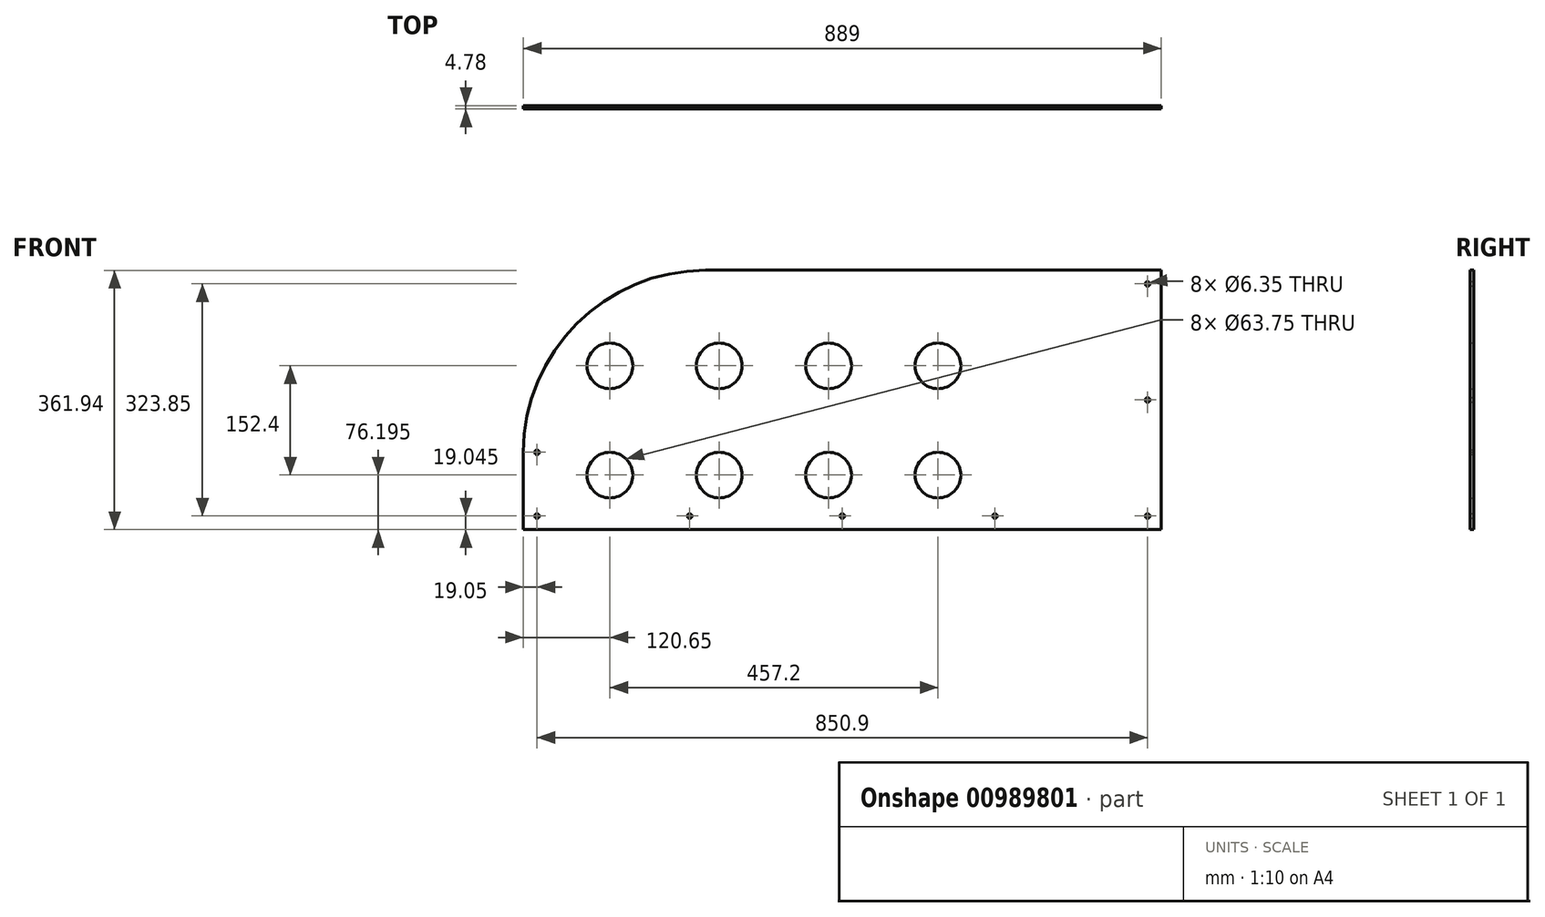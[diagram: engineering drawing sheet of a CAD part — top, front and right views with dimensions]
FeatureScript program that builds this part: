
annotation { "Feature Type Name" : "Feature", "Feature Type Description" : "" }
export const myFeature = defineFeature(function(context is Context, id is Id, definition is map)
    precondition{}
    {
        {
            var Q0;
            Q0=qCreatedBy(makeId("Front.planeOp"),FACE);
            var sketch = newSketch(context, id + "F0", { "sketchPlane" : qUnion([Q0])});
            skLineSegment(sketch, "E0.bottom", {"start": v(-190.5, 180.98) * mm, "end": v(444.5, 180.98) * mm});
            skLineSegment(sketch, "E0.top", {"start": v(-444.5, -180.98) * mm, "end": v(444.5, -180.98) * mm});
            skLineSegment(sketch, "E0.left", {"start": v(-444.5, -73.02) * mm, "end": v(-444.5, -180.98) * mm});
            skLineSegment(sketch, "E0.right", {"start": v(444.5, 180.98) * mm, "end": v(444.5, -180.98) * mm});
            skCircle(sketch, "E1", {"center": v(-323.85, 47.62) * mm, "radius": 31.88 * mm});
            skCircle(sketch, "E2.0.1.0", {"center": v(-323.85, -104.78) * mm, "radius": 31.88 * mm});
            skCircle(sketch, "E2.1.0.0", {"center": v(-171.45, 47.62) * mm, "radius": 31.88 * mm});
            skCircle(sketch, "E2.1.1.0", {"center": v(-171.45, -104.78) * mm, "radius": 31.88 * mm});
            skCircle(sketch, "E2.2.0.0", {"center": v(-19.05, 47.62) * mm, "radius": 31.88 * mm});
            skCircle(sketch, "E2.2.1.0", {"center": v(-19.05, -104.78) * mm, "radius": 31.88 * mm});
            skCircle(sketch, "E2.3.0.0", {"center": v(133.35, 47.62) * mm, "radius": 31.88 * mm});
            skCircle(sketch, "E2.3.1.0", {"center": v(133.35, -104.78) * mm, "radius": 31.88 * mm});
            skLineSegment(sketch, "E2.direction1", {"start": v(-323.85, 47.62) * mm, "end": v(-171.45, 47.62) * mm, "construction": true});
            skLineSegment(sketch, "E2.direction2", {"start": v(-323.85, 47.62) * mm, "end": v(-323.85, -104.78) * mm, "construction": true});
            skPoint(sketch, "E3.visualSharp", {"position": v(-444.5, 180.98) * mm});
            skArc(sketch, "E3.filletArc", {"start": v(-190.5, 180.98) * mm, "mid": v(-370.1, 106.58) * mm, "end": v(-444.5, -73.02) * mm});
            skCircle(sketch, "E4", {"center": v(-425.45, -161.92) * mm, "radius": 3.18 * mm});
            skCircle(sketch, "E5.1.0.0", {"center": v(-212.73, -161.92) * mm, "radius": 3.18 * mm});
            skCircle(sketch, "E5.2.0.0", {"center": v(0, -161.92) * mm, "radius": 3.18 * mm});
            skCircle(sketch, "E5.3.0.0", {"center": v(212.72, -161.92) * mm, "radius": 3.18 * mm});
            skCircle(sketch, "E5.4.0.0", {"center": v(425.45, -161.92) * mm, "radius": 3.18 * mm});
            skLineSegment(sketch, "E5.direction1", {"start": v(-425.45, -161.92) * mm, "end": v(-212.73, -161.92) * mm, "construction": true});
            skCircle(sketch, "E6", {"center": v(-425.45, -73.02) * mm, "radius": 3.18 * mm});
            skCircle(sketch, "E7.0.1.0", {"center": v(425.45, 0) * mm, "radius": 3.18 * mm});
            skCircle(sketch, "E7.0.2.0", {"center": v(425.45, 161.93) * mm, "radius": 3.18 * mm});
            skLineSegment(sketch, "E7.direction1", {"start": v(425.45, -161.92) * mm, "end": v(450.85, -161.92) * mm, "construction": true});
            skLineSegment(sketch, "E7.direction2", {"start": v(425.45, -161.92) * mm, "end": v(425.45, 0) * mm, "construction": true});
            skSolve(sketch);
        }
        {
            var Q0;
            Q0=makeQuery(id+"F0.imprint","IMPRINT",FACE,{"disambiguationData":[TD([[makeQuery(id+"F0.imprint","IMPRINT",EDGE,{"derivedFrom":sQuery(id+"F0.wireOp",EDGE,"E0.bottom")}),-1.0]])]});
            extrude(context, id + "F1", {"entities" : qUnion([Q0]), "depth" : 4.78 * mm, "offsetDistance" : 25.4 * mm});
        }
    });
